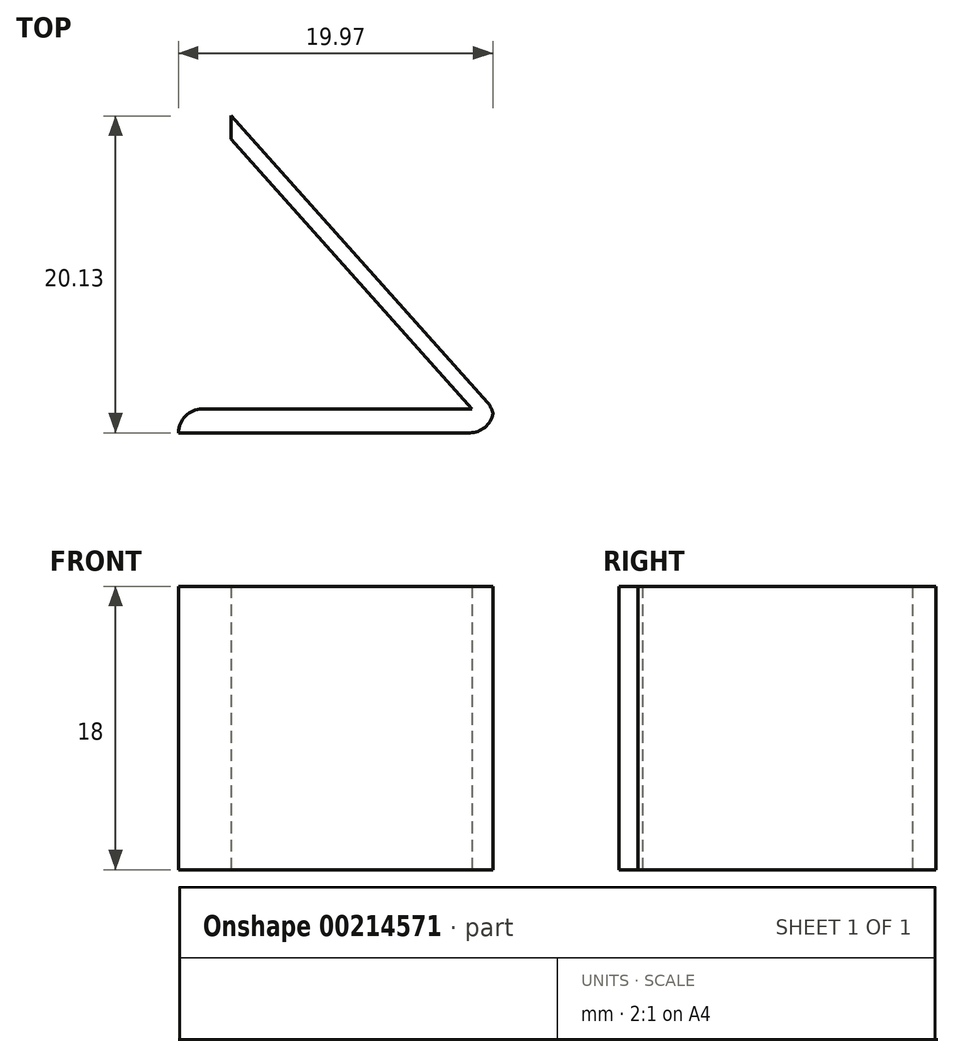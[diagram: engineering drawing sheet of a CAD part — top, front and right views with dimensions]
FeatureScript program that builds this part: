
annotation { "Feature Type Name" : "Feature", "Feature Type Description" : "" }
export const myFeature = defineFeature(function(context is Context, id is Id, definition is map)
    precondition{}
    {
        {
            var Q0;
            Q0=qCreatedBy(makeId("Top.planeOp"),FACE);
            var sketch = newSketch(context, id + "F0", { "sketchPlane" : qUnion([Q0])});
            skLineSegment(sketch, "E0.bottom", {"start": v(-34.85, 48.22) * mm, "end": v(-16.19, 48.22) * mm});
            skLineSegment(sketch, "E0.top", {"start": v(-34.85, 46.72) * mm, "end": v(-14.85, 46.72) * mm});
            skLineSegment(sketch, "E0.left", {"start": v(-34.85, 48.22) * mm, "end": v(-34.85, 46.72) * mm});
            skLineSegment(sketch, "E0.right", {"start": v(-14.85, 48.22) * mm, "end": v(-14.85, 46.72) * mm});
            skLineSegment(sketch, "E1", {"start": v(-31.52, 65.36) * mm, "end": v(-16.19, 48.22) * mm});
            skLineSegment(sketch, "E2", {"start": v(-14.85, 48.22) * mm, "end": v(-31.51, 66.85) * mm});
            skLineSegment(sketch, "E3", {"start": v(-31.52, 65.36) * mm, "end": v(-31.51, 66.85) * mm});
            skSolve(sketch);
        }
        {
            var Q0;
            Q0 = qSketchRegion(id + "F0", true);
            extrude(context, id + "F1", {"entities" : qUnion([Q0]), "depth" : 18 * mm});
        }
        {
            var Q0;
            Q0=makeQuery(id+"F1.opExtrude","SWEPT_EDGE",EDGE,{"disambiguationData":[OSD([sQuery(id+"F0.wireOp",EDGE,"E0.top"),sQuery(id+"F0.wireOp",EDGE,"E0.right")])]});
            var Q1;
            Q1=makeQuery(id+"F1.opExtrude","SWEPT_EDGE",EDGE,{"disambiguationData":[OSD([sQuery(id+"F0.wireOp",EDGE,"E0.right"),sQuery(id+"F0.wireOp",EDGE,"E2")])]});
            var Q2;
            Q2=makeQuery(id+"F1.opExtrude","SWEPT_EDGE",EDGE,{"disambiguationData":[OSD([sQuery(id+"F0.wireOp",EDGE,"E0.bottom"),sQuery(id+"F0.wireOp",EDGE,"E0.left")])]});
            fillet(context, id + "F2", {"entities" : qUnion([Q0, Q1, Q2]), "radius" : 1.5 * mm, "tangentPropagation" : true, "allowEdgeOverflow" : false});
        }
    });
